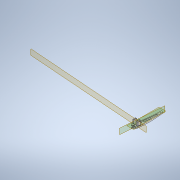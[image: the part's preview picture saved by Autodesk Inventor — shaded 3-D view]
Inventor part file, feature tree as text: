
AUTODESK INVENTOR PART (.ipt)
format: ipt  version: 2020.3 (Build 243373000, 373)  size: 382,976 bytes
history: native  units: mm
features: other x3, plane x3, sketch x2
ambient origin geometry x8: Origin, YZ Plane, XZ Plane, XY Plane, X Axis, Y Axis, Z Axis, Center Point
bodies: Solid1 (feature_tree)
feature tree (8):
  other  "LegEnd_Right_v2.ipt"
  plane  "Work Plane1"
  plane  "Work Plane2"
  plane  "Work Plane3"
  other  "Solid1::LegEnd_Right_v2.ipt"
  other  "TaggingFeature1"
  sketch  "Sketch1"  dims[d0=10.0mm]
  sketch  "Sketch3"  dims[d1=90.0deg d2=90.0deg d3=-7.5mm]
